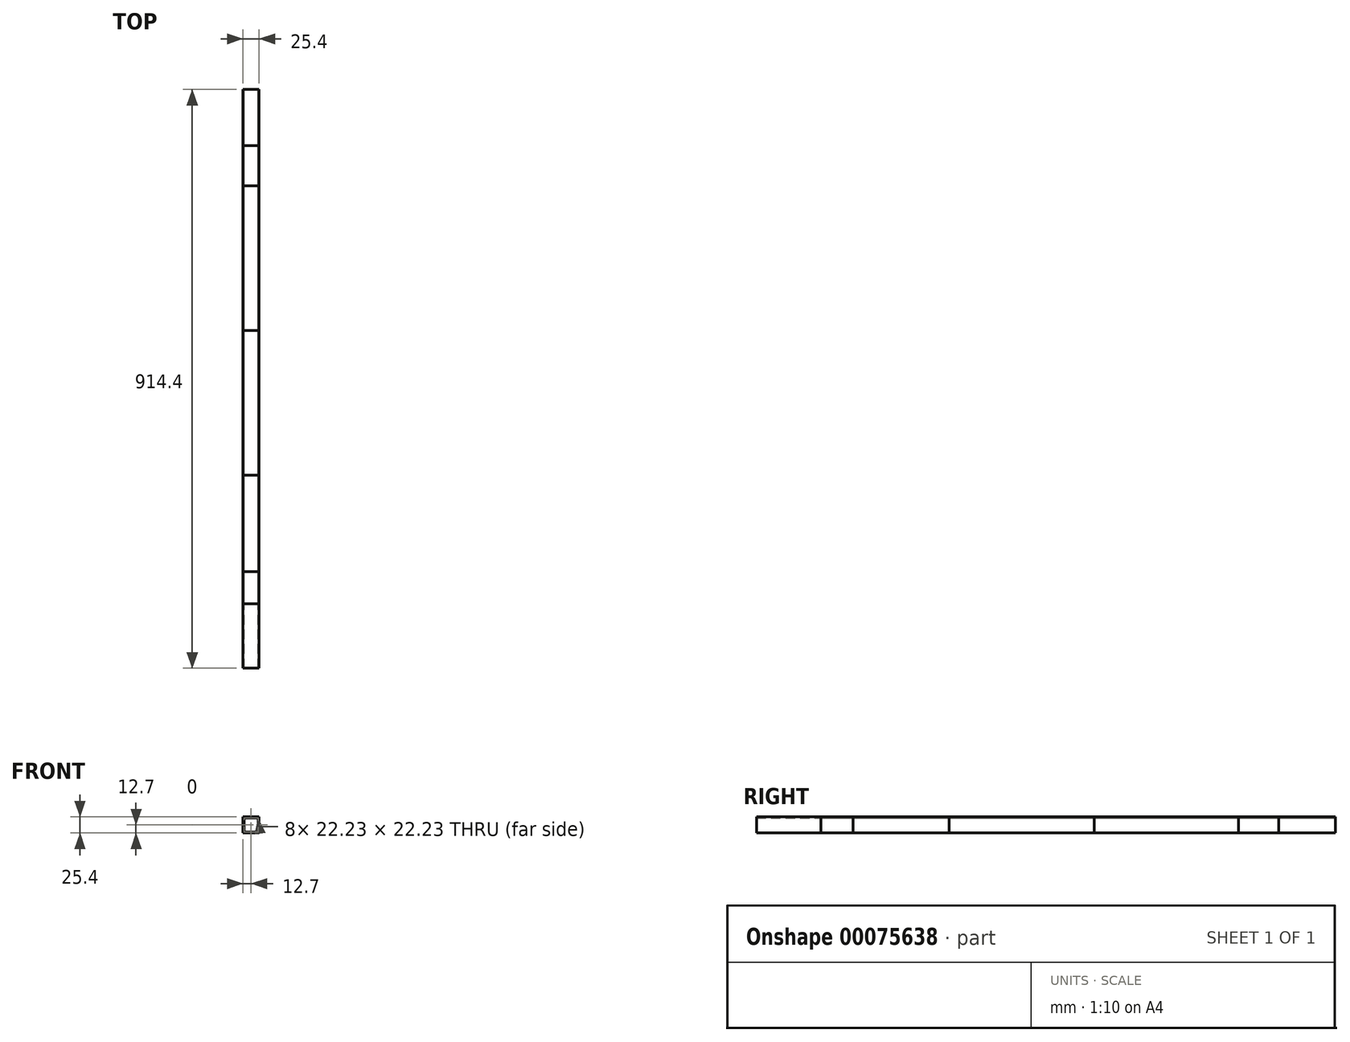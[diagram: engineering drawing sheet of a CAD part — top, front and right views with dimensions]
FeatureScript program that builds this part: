
annotation { "Feature Type Name" : "Feature", "Feature Type Description" : "" }
export const myFeature = defineFeature(function(context is Context, id is Id, definition is map)
    precondition{}
    {
        {
            var Q0;
            Q0=qCreatedBy(makeId("Front.planeOp"),FACE);
            var sketch = newSketch(context, id + "F0", { "sketchPlane" : qUnion([Q0])});
            skLineSegment(sketch, "E0.bottom", {"start": v(0, 0) * mm, "end": v(25.4, 0) * mm});
            skLineSegment(sketch, "E0.top", {"start": v(0, 25.4) * mm, "end": v(25.4, 25.4) * mm});
            skLineSegment(sketch, "E0.left", {"start": v(0, 0) * mm, "end": v(0, 25.4) * mm});
            skLineSegment(sketch, "E0.right", {"start": v(25.4, 0) * mm, "end": v(25.4, 25.4) * mm});
            skLineSegment(sketch, "E1.bottom", {"start": v(1.59, 1.59) * mm, "end": v(23.81, 1.59) * mm});
            skLineSegment(sketch, "E1.top", {"start": v(1.59, 23.81) * mm, "end": v(23.81, 23.81) * mm});
            skLineSegment(sketch, "E1.left", {"start": v(1.59, 1.59) * mm, "end": v(1.59, 23.81) * mm});
            skLineSegment(sketch, "E1.right", {"start": v(23.81, 1.59) * mm, "end": v(23.81, 23.81) * mm});
            skSolve(sketch);
        }
        {
            var Q0;
            Q0=makeQuery(id+"F0.imprint","IMPRINT",FACE,{"disambiguationData":[TD([[makeQuery(id+"F0.imprint","IMPRINT",EDGE,{"derivedFrom":sQuery(id+"F0.wireOp",EDGE,"E0.bottom")}),1.0]])]});
            extrude(context, id + "F1", {"entities" : qUnion([Q0]), "depth" : 914.4 * mm});
        }
        {
            var Q0;
            Q0=qSketchRegion(id+"F0",true);
            extrude(context, id + "F2", {"entities" : qUnion([Q0]), "depth" : 152.4 * mm});
        }
        {
            var Q0;
            Q0=qSketchRegion(id+"F0",true);
            extrude(context, id + "F3", {"entities" : qUnion([Q0]), "depth" : 381 * mm});
        }
        {
            var Q0;
            Q0=qSketchRegion(id+"F0",true);
            extrude(context, id + "F4", {"entities" : qUnion([Q0]), "depth" : 381 * mm});
        }
        {
            var Q0;
            Q0=qSketchRegion(id+"F0",true);
            extrude(context, id + "F5", {"entities" : qUnion([Q0]), "depth" : 609.6 * mm});
        }
        {
            var Q0;
            Q0=qSketchRegion(id+"F0",true);
            extrude(context, id + "F6", {"entities" : qUnion([Q0]), "depth" : 812.8 * mm});
        }
        {
            var Q0;
            Q0=qSketchRegion(id+"F0",true);
            extrude(context, id + "F7", {"entities" : qUnion([Q0]), "depth" : 88.9 * mm});
        }
        {
            var Q0;
            Q0=qSketchRegion(id+"F0",true);
            extrude(context, id + "F8", {"entities" : qUnion([Q0]), "depth" : 762 * mm});
        }
    });
